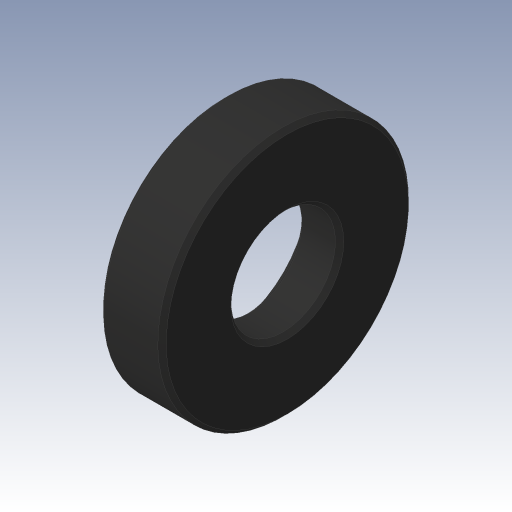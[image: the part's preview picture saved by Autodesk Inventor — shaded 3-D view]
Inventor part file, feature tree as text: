
AUTODESK INVENTOR PART (.ipt)
format: ipt  version: 2023.3 (Build 273359000, 359)  size: 150,528 bytes
history: native  units: in
note: dims shown in document units (in); Inventor stores cm internally (conversion verified against a paired STEP export)
features: revolve x1, chamfer x1, sketch x1
ambient origin geometry x8: Origin, YZ Plane, XZ Plane, XY Plane, X Axis, Y Axis, Z Axis, Center Point
bodies: Body1 (feature_tree)
feature tree (3):
  revolve  "Umdrehung1"
  chamfer  "Fase1"  Distance=0.1969in
  sketch  "Skizze3"  dims[d4=0.4724in d5=0.1969in d6=0.1181in d7=0.0394in d9=0.315in d10=90.0deg d11=0.0079in d12=0.0787in d13=45.0deg]
